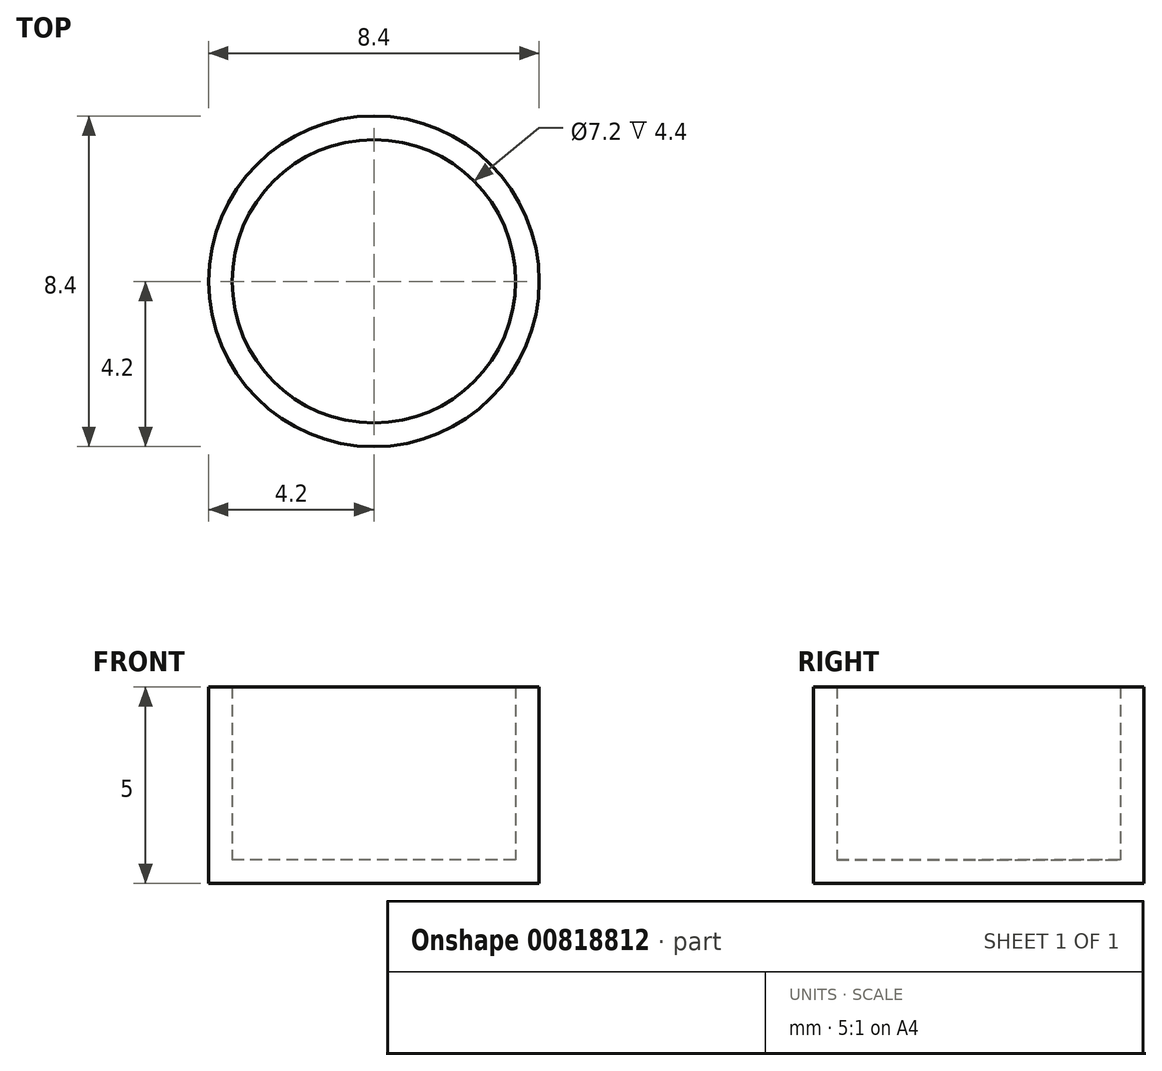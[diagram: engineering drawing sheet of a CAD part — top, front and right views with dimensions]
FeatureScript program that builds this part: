
annotation { "Feature Type Name" : "Feature", "Feature Type Description" : "" }
export const myFeature = defineFeature(function(context is Context, id is Id, definition is map)
    precondition{}
    {
        {
            var Q0;
            Q0=qCreatedBy(makeId("Top.planeOp"),FACE);
            var sketch = newSketch(context, id + "F0", { "sketchPlane" : qUnion([Q0])});
            skCircle(sketch, "E0", {"center": v(0, 0) * mm, "radius": 4.2 * mm});
            skSolve(sketch);
        }
        {
            var Q0;
            Q0 = qSketchRegion(id + "F0", true);
            extrude(context, id + "F1", {"entities" : qUnion([Q0]), "depth" : 5 * mm, "offsetDistance" : 25 * mm});
        }
        {
            var Q0;
            Q0=makeQuery(id+"F1.opExtrude","CAP_FACE",FACE,{"disambiguationData":[OSD([sQuery(id+"F0.wireOp",EDGE,"E0")])],"isStart":false});
            shell(context, id + "F2", {"entities" : qUnion([Q0]), "thickness" : .6 * mm});
        }
    });
